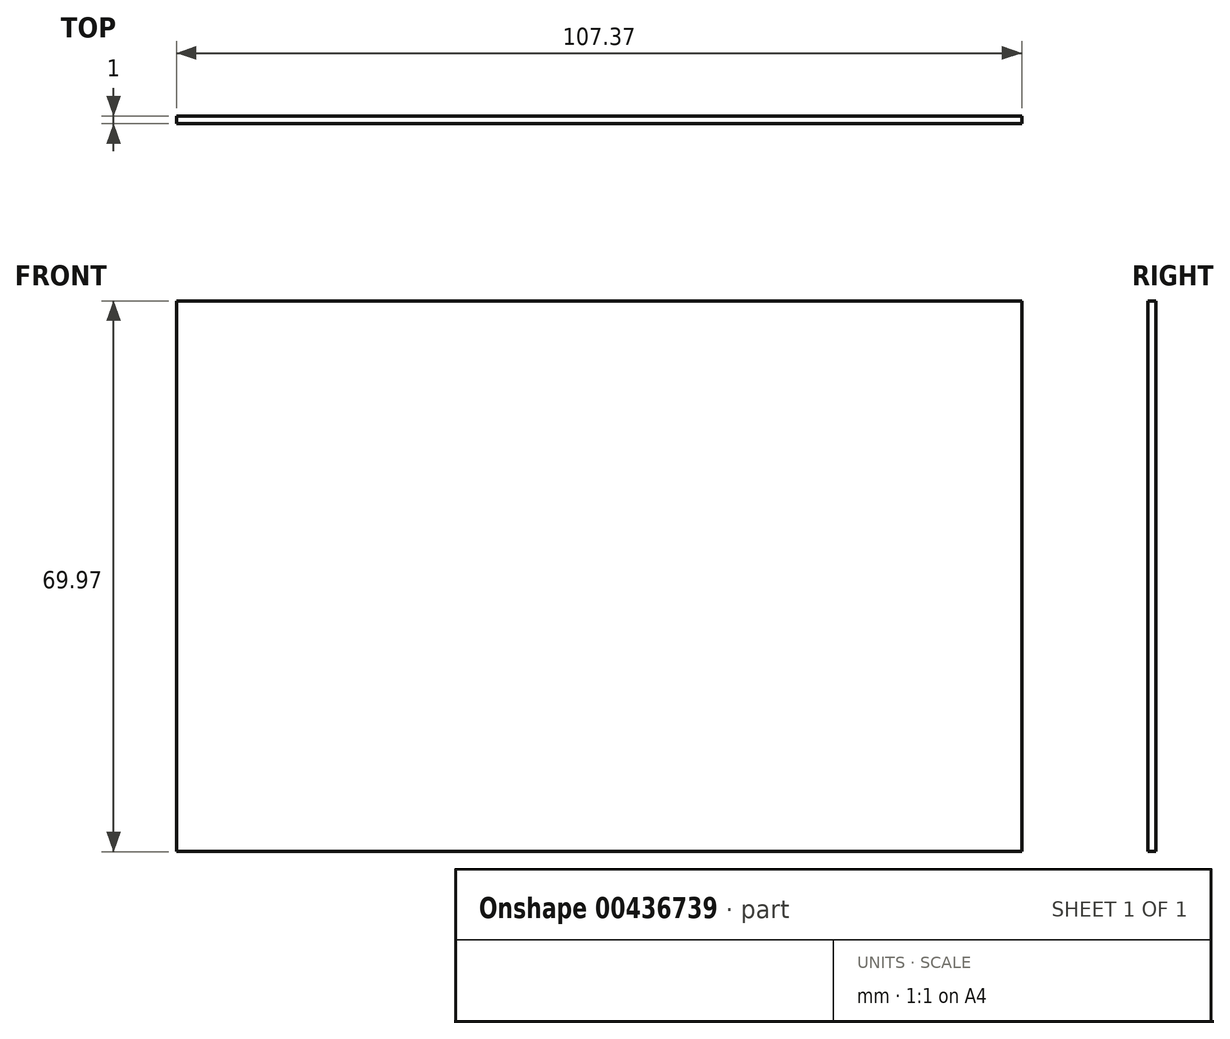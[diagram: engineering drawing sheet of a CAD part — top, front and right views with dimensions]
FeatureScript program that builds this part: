
annotation { "Feature Type Name" : "Feature", "Feature Type Description" : "" }
export const myFeature = defineFeature(function(context is Context, id is Id, definition is map)
    precondition{}
    {
        {
            var Q0;
            Q0=qCreatedBy(makeId("Front.planeOp"),FACE);
            var sketch = newSketch(context, id + "F0", { "sketchPlane" : qUnion([Q0])});
            skLineSegment(sketch, "E0.bottom", {"start": v(-55.29, 20.42) * mm, "end": v(52.08, 20.42) * mm});
            skLineSegment(sketch, "E0.top", {"start": v(-55.29, -49.55) * mm, "end": v(52.08, -49.55) * mm});
            skLineSegment(sketch, "E0.left", {"start": v(-55.29, 20.42) * mm, "end": v(-55.29, -49.55) * mm});
            skLineSegment(sketch, "E0.right", {"start": v(52.08, 20.42) * mm, "end": v(52.08, -49.55) * mm});
            skSolve(sketch);
        }
        {
            var Q0;
            Q0 = qSketchRegion(id + "F0", true);
            extrude(context, id + "F1", {"entities" : qUnion([Q0]), "depth" : 1 * mm, "offsetDistance" : 25 * mm});
        }
    });
